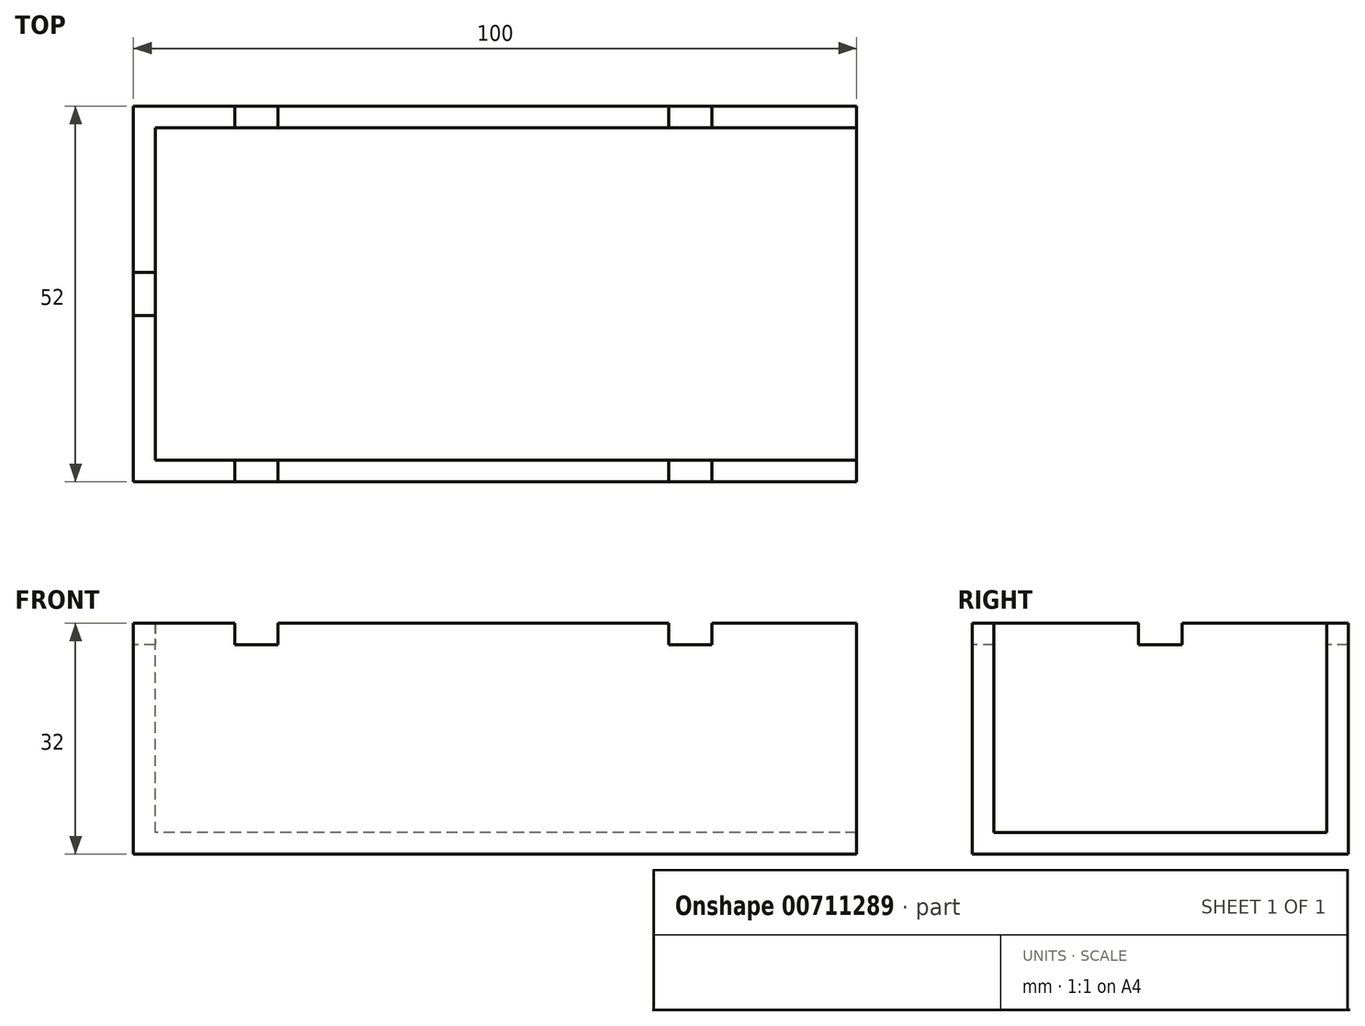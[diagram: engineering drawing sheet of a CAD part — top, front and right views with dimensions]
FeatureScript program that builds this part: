
annotation { "Feature Type Name" : "Feature", "Feature Type Description" : "" }
export const myFeature = defineFeature(function(context is Context, id is Id, definition is map)
    precondition{}
    {
        {
            var Q0;
            Q0=qCreatedBy(makeId("Top.planeOp"),FACE);
            var sketch = newSketch(context, id + "F0", { "sketchPlane" : qUnion([Q0])});
            skLineSegment(sketch, "E0.bottom", {"start": v(50, -26) * mm, "end": v(-50, -26) * mm});
            skLineSegment(sketch, "E0.top", {"start": v(50, 26) * mm, "end": v(-50, 26) * mm});
            skLineSegment(sketch, "E0.left", {"start": v(50, -26) * mm, "end": v(50, 26) * mm});
            skLineSegment(sketch, "E0.right", {"start": v(-50, -26) * mm, "end": v(-50, 26) * mm});
            skPoint(sketch, "E0.middle", {"position": v(0, 0) * mm});
            skSolve(sketch);
        }
        {
            var Q0;
            Q0 = qSketchRegion(id + "F0", true);
            extrude(context, id + "F1", {"entities" : qUnion([Q0]), "depth" : 32 * mm, "offsetDistance" : 25 * mm});
        }
        {
            var Q0;
            Q0=makeQuery(id+"F1.opExtrude","CAP_FACE",FACE,{"disambiguationData":[OSD([sQuery(id+"F0.wireOp",EDGE,"E0.bottom"),sQuery(id+"F0.wireOp",EDGE,"E0.top"),sQuery(id+"F0.wireOp",EDGE,"E0.left"),sQuery(id+"F0.wireOp",EDGE,"E0.right")])],"isStart":false});
            var sketch = newSketch(context, id + "F2", { "sketchPlane" : qUnion([Q0])});
            skPoint(sketch, "E1", {"position": v(50, 23) * mm});
            skLineSegment(sketch, "E2.bottom", {"start": v(50, 23) * mm, "end": v(-47, 23) * mm});
            skLineSegment(sketch, "E2.top", {"start": v(50, -23) * mm, "end": v(-47, -23) * mm});
            skLineSegment(sketch, "E2.left", {"start": v(50, 23) * mm, "end": v(50, -23) * mm});
            skLineSegment(sketch, "E2.right", {"start": v(-47, 23) * mm, "end": v(-47, -23) * mm});
            skSolve(sketch);
        }
        {
            var Q0;
            Q0 = qSketchRegion(id + "F2", true);
            extrude(context, id + "F3", {"entities" : qUnion([Q0]), "operationType" : NewBodyOperationType.REMOVE, "oppositeDirection" : true, "depth" : 29 * mm, "offsetDistance" : 25 * mm});
        }
        {
            var Q0;
            Q0=makeQuery(id+"F1.opExtrude","SWEPT_FACE",FACE,{"disambiguationData":[OSD([sQuery(id+"F0.wireOp",EDGE,"E0.bottom")])]});
            var sketch = newSketch(context, id + "F4", { "sketchPlane" : qUnion([Q0])});
            skPoint(sketch, "E3", {"position": v(30, 32) * mm});
            skPoint(sketch, "E4", {"position": v(-30, 32) * mm});
            skLineSegment(sketch, "E5.bottom", {"start": v(-30, 32) * mm, "end": v(-36, 32) * mm});
            skLineSegment(sketch, "E5.top", {"start": v(-30, 29) * mm, "end": v(-36, 29) * mm});
            skLineSegment(sketch, "E5.left", {"start": v(-30, 32) * mm, "end": v(-30, 29) * mm});
            skLineSegment(sketch, "E5.right", {"start": v(-36, 32) * mm, "end": v(-36, 29) * mm});
            skSolve(sketch);
        }
        {
            var Q0;
            Q0 = qSketchRegion(id + "F4", true);
            extrude(context, id + "F5", {"entities" : qUnion([Q0]), "operationType" : NewBodyOperationType.REMOVE, "endBound" : BoundingType.THROUGH_ALL, "oppositeDirection" : true, "depth" : 25 * mm, "offsetDistance" : 25 * mm});
        }
        {
            var Q0;
            Q0=makeQuery(id+"F1.opExtrude","SWEPT_FACE",FACE,{"disambiguationData":[OSD([sQuery(id+"F0.wireOp",EDGE,"E0.bottom")])]});
            var sketch = newSketch(context, id + "F6", { "sketchPlane" : qUnion([Q0])});
            skPoint(sketch, "E6", {"position": v(30, 32) * mm});
            skLineSegment(sketch, "E7.bottom", {"start": v(30, 32) * mm, "end": v(24, 32) * mm});
            skLineSegment(sketch, "E7.top", {"start": v(30, 29) * mm, "end": v(24, 29) * mm});
            skLineSegment(sketch, "E7.left", {"start": v(30, 32) * mm, "end": v(30, 29) * mm});
            skLineSegment(sketch, "E7.right", {"start": v(24, 32) * mm, "end": v(24, 29) * mm});
            skSolve(sketch);
        }
        {
            var Q0;
            Q0 = qSketchRegion(id + "F6", true);
            extrude(context, id + "F7", {"entities" : qUnion([Q0]), "operationType" : NewBodyOperationType.REMOVE, "endBound" : BoundingType.THROUGH_ALL, "oppositeDirection" : true, "depth" : 25 * mm, "offsetDistance" : 25 * mm});
        }
        {
            var Q0;
            Q0=makeQuery(id+"F1.opExtrude","SWEPT_FACE",FACE,{"disambiguationData":[OSD([sQuery(id+"F0.wireOp",EDGE,"E0.right")])]});
            var sketch = newSketch(context, id + "F8", { "sketchPlane" : qUnion([Q0])});
            skLineSegment(sketch, "E8.bottom", {"start": v(3, 35) * mm, "end": v(-3, 35) * mm});
            skLineSegment(sketch, "E8.top", {"start": v(3, 29) * mm, "end": v(-3, 29) * mm});
            skLineSegment(sketch, "E8.left", {"start": v(3, 35) * mm, "end": v(3, 29) * mm});
            skLineSegment(sketch, "E8.right", {"start": v(-3, 35) * mm, "end": v(-3, 29) * mm});
            skPoint(sketch, "E8.middle", {"position": v(0, 32) * mm});
            skSolve(sketch);
        }
        {
            var Q0;
            {var subQ0=sQuery(id+"F8.wireOp",EDGE,"E8.top");Q0=makeQuery(id+"F8.imprint","IMPRINT",FACE,{"disambiguationData":[TD([[makeQuery(id+"F8.imprint","IMPRINT",EDGE,{"derivedFrom":subQ0}),-1.0]])]});}
            extrude(context, id + "F9", {"entities" : qUnion([Q0]), "operationType" : NewBodyOperationType.REMOVE, "endBound" : BoundingType.THROUGH_ALL, "oppositeDirection" : true, "depth" : 25 * mm, "offsetDistance" : 25 * mm});
        }
    });
